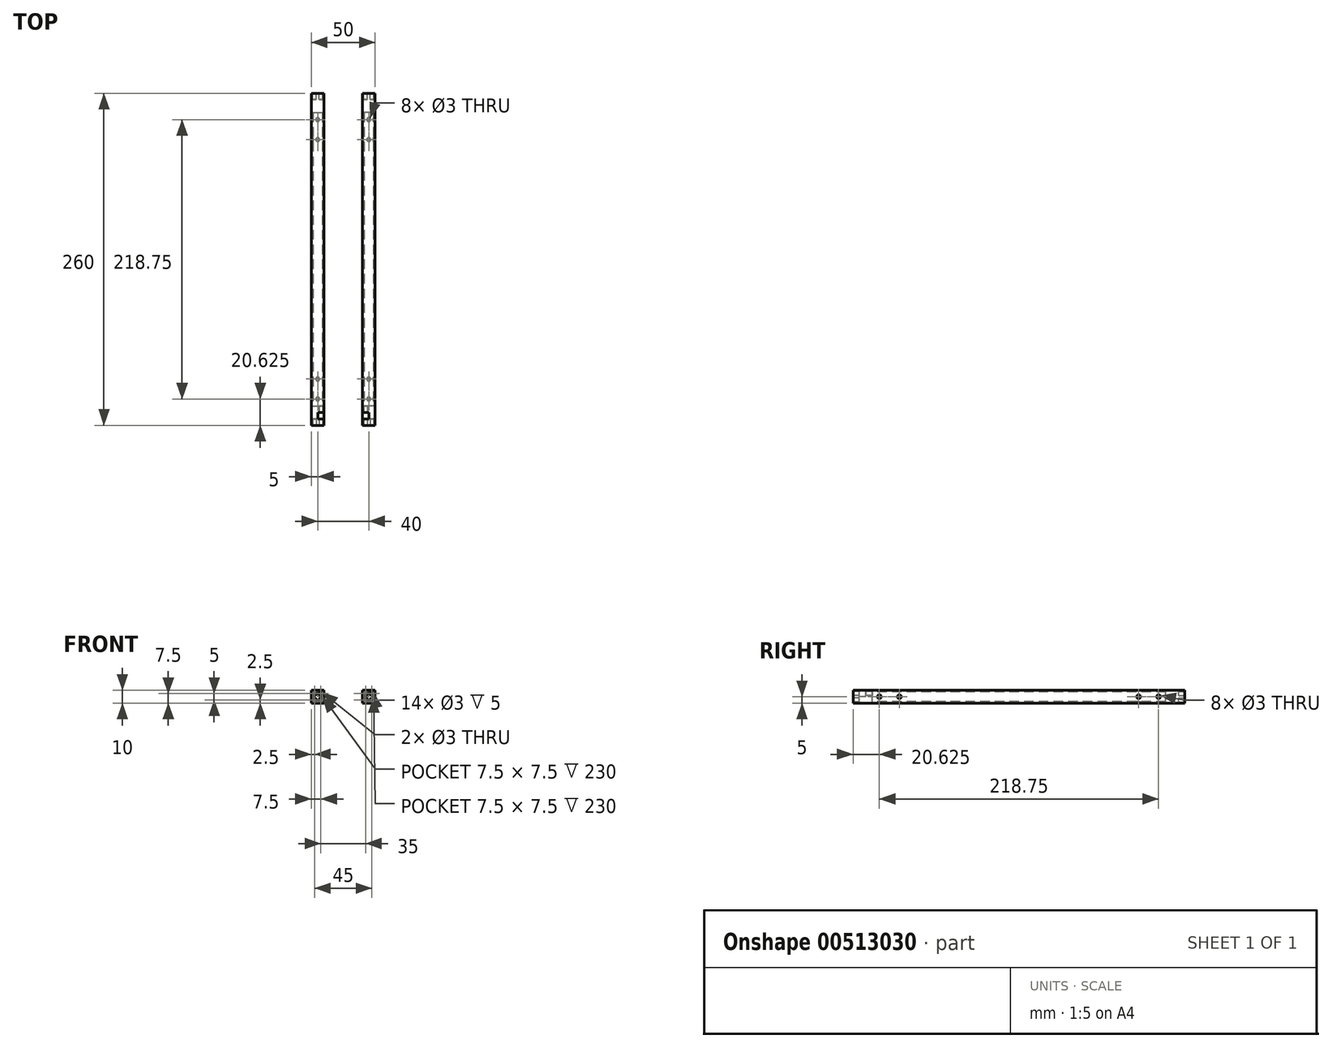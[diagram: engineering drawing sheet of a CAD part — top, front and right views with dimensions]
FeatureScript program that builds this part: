
annotation { "Feature Type Name" : "Feature", "Feature Type Description" : "" }
export const myFeature = defineFeature(function(context is Context, id is Id, definition is map)
    precondition{}
    {
        {
            var Q0;
            Q0=qCreatedBy(makeId("Front.planeOp"),FACE);
            var sketch = newSketch(context, id + "F0", { "sketchPlane" : qUnion([Q0])});
            skLineSegment(sketch, "E0.bottom", {"start": v(0, 0) * mm, "end": v(-10, 0) * mm});
            skLineSegment(sketch, "E0.top", {"start": v(0, 10) * mm, "end": v(-10, 10) * mm});
            skLineSegment(sketch, "E0.left", {"start": v(0, 0) * mm, "end": v(0, 10) * mm});
            skLineSegment(sketch, "E0.right", {"start": v(-10, 0) * mm, "end": v(-10, 10) * mm});
            skLineSegment(sketch, "E1.bottom", {"start": v(-1.25, 1.25) * mm, "end": v(-8.75, 1.25) * mm});
            skLineSegment(sketch, "E1.top", {"start": v(-1.25, 8.75) * mm, "end": v(-8.75, 8.75) * mm});
            skLineSegment(sketch, "E1.left", {"start": v(-1.25, 1.25) * mm, "end": v(-1.25, 8.75) * mm});
            skLineSegment(sketch, "E1.right", {"start": v(-8.75, 1.25) * mm, "end": v(-8.75, 8.75) * mm});
            skPoint(sketch, "E1.middle", {"position": v(-5, 5) * mm});
            skPoint(sketch, "E1.middle.positionSnap0", {"position": v(0, 5) * mm});
            skPoint(sketch, "E1.middle.positionSnap1", {"position": v(-5, 10) * mm});
            skPoint(sketch, "E1.centerSnap0", {"position": v(0, 5) * mm});
            skPoint(sketch, "E1.centerSnap1", {"position": v(-5, 10) * mm});
            skSolve(sketch);
        }
        {
            var Q0;
            Q0=makeQuery(id+"F0.imprint","IMPRINT",FACE,{"disambiguationData":[TD([[makeQuery(id+"F0.imprint","IMPRINT",EDGE,{"derivedFrom":sQuery(id+"F0.wireOp",EDGE,"E0.bottom")}),-1.0]])]});
            extrude(context, id + "F1", {"entities" : qUnion([Q0]), "oppositeDirection" : true, "depth" : 250 * mm});
        }
        {
            var Q0;
            Q0=makeQuery(id+"F0.imprint","IMPRINT",FACE,{"disambiguationData":[TD([[makeQuery(id+"F0.imprint","IMPRINT",EDGE,{"derivedFrom":sQuery(id+"F0.wireOp",EDGE,"E1.bottom")}),-1.0]])]});
            var Q1;
            Q1=makeQuery(id+"F0.imprint","IMPRINT",FACE,{"disambiguationData":[TD([[makeQuery(id+"F0.imprint","IMPRINT",EDGE,{"derivedFrom":sQuery(id+"F0.wireOp",EDGE,"E0.bottom")}),-1.0]])]});
            extrude(context, id + "F2", {"entities" : qUnion([Q0, Q1]), "operationType" : NewBodyOperationType.ADD, "depth" : 5 * mm});
        }
        {
            var Q0;
            Q0=makeQuery(id+"F2.opExtrude","CAP_FACE",FACE,{"disambiguationData":[OSD([sQuery(id+"F0.wireOp",EDGE,"E0.bottom"),sQuery(id+"F0.wireOp",EDGE,"E0.top"),sQuery(id+"F0.wireOp",EDGE,"E0.left"),sQuery(id+"F0.wireOp",EDGE,"E0.right")])],"isStart":false});
            var sketch = newSketch(context, id + "F3", { "sketchPlane" : qUnion([Q0])});
            skLineSegment(sketch, "E2", {"start": v(-5, 10) * mm, "end": v(-5, 5) * mm});
            skPoint(sketch, "E2.endSnap0", {"position": v(0, 5) * mm});
            skLineSegment(sketch, "E3", {"start": v(-5, 5) * mm, "end": v(0, 5) * mm});
            skLineSegment(sketch, "E4", {"start": v(-5, 5) * mm, "end": v(-5, 0) * mm});
            skLineSegment(sketch, "E5", {"start": v(-5, 5) * mm, "end": v(-10, 5) * mm});
            skCircle(sketch, "E6", {"center": v(-2.5, 7.5) * mm, "radius": 1.5 * mm});
            skPoint(sketch, "E6.centerSnap0", {"position": v(-2.5, 5) * mm});
            skPoint(sketch, "E6.centerSnap1", {"position": v(-5, 7.5) * mm});
            skCircle(sketch, "E7", {"center": v(-2.5, 2.5) * mm, "radius": 1.5 * mm});
            skPoint(sketch, "E7.centerSnap0", {"position": v(-5, 2.5) * mm});
            skCircle(sketch, "E8", {"center": v(-7.5, 2.5) * mm, "radius": 1.5 * mm});
            skPoint(sketch, "E8.centerSnap0", {"position": v(-7.5, 5) * mm});
            skCircle(sketch, "E9", {"center": v(-7.5, 7.5) * mm, "radius": 1.5 * mm});
            skSolve(sketch);
        }
        {
            var Q0;
            {var subQ0=sQuery(id+"F0.wireOp",EDGE,"E0.top");Q0=makeQuery(id+"F2.boolean.opBoolean","MERGE",FACE,{"derivedFrom":[makeQuery(id+"F1.opExtrude","SWEPT_FACE",FACE,{"disambiguationData":[OSD([subQ0])]}),makeQuery(id+"F2.opExtrude","SWEPT_FACE",FACE,{"disambiguationData":[OSD([subQ0])]})]});}
            var sketch = newSketch(context, id + "F4", { "sketchPlane" : qUnion([Q0])});
            skLineSegment(sketch, "E10.bottom", {"start": v(0, 0) * mm, "end": v(-10, 0) * mm});
            skLineSegment(sketch, "E10.top", {"start": v(0, 250) * mm, "end": v(-10, 250) * mm});
            skLineSegment(sketch, "E10.left", {"start": v(0, 0) * mm, "end": v(0, 250) * mm});
            skLineSegment(sketch, "E10.right", {"start": v(-10, 0) * mm, "end": v(-10, 250) * mm});
            skLineSegment(sketch, "E11", {"start": v(0, 125) * mm, "end": v(-10, 125) * mm});
            skSolve(sketch);
        }
        {
            var Q0;
            {var subQ0=sQuery(id+"F4.wireOp",EDGE,"E10.top");Q0=makeQuery(id+"F4.imprint","IMPRINT",FACE,{"disambiguationData":[TD([[makeQuery(id+"F4.imprint","IMPRINT",EDGE,{"derivedFrom":subQ0}),1.0]])]});}
            extrude(context, id + "F5", {"entities" : qUnion([Q0]), "operationType" : NewBodyOperationType.REMOVE, "oppositeDirection" : true, "depth" : 25 * mm});
        }
        {
            var Q0;
            Q0=makeQuery(id+"F3.imprint","IMPRINT",FACE,{"disambiguationData":[TD([[makeQuery(id+"F3.imprint","IMPRINT",EDGE,{"derivedFrom":sQuery(id+"F3.wireOp",EDGE,"E7")}),1.0]])]});
            var Q1;
            Q1=makeQuery(id+"F3.imprint","IMPRINT",FACE,{"disambiguationData":[TD([[makeQuery(id+"F3.imprint","IMPRINT",EDGE,{"derivedFrom":sQuery(id+"F3.wireOp",EDGE,"E6")}),1.0]])]});
            var Q2;
            Q2=makeQuery(id+"F3.imprint","IMPRINT",FACE,{"disambiguationData":[TD([[makeQuery(id+"F3.imprint","IMPRINT",EDGE,{"derivedFrom":sQuery(id+"F3.wireOp",EDGE,"E8")}),1.0]])]});
            extrude(context, id + "F6", {"entities" : qUnion([Q0, Q1, Q2]), "operationType" : NewBodyOperationType.REMOVE, "oppositeDirection" : true, "depth" : 5 * mm});
        }
        {
            var Q0;
            Q0=makeQuery(id+"F0.imprint","IMPRINT",FACE,{"disambiguationData":[TD([[makeQuery(id+"F0.imprint","IMPRINT",EDGE,{"derivedFrom":sQuery(id+"F0.wireOp",EDGE,"E1.bottom")}),-1.0]])]});
            extrude(context, id + "F7", {"entities" : qUnion([Q0]), "operationType" : NewBodyOperationType.ADD, "oppositeDirection" : true, "depth" : 10 * mm});
        }
        {
            var Q0;
            {var subQ0=sQuery(id+"F0.wireOp",EDGE,"E0.left");Q0=makeQuery(id+"F2.boolean.opBoolean","MERGE",FACE,{"derivedFrom":[makeQuery(id+"F1.opExtrude","SWEPT_FACE",FACE,{"disambiguationData":[OSD([subQ0])]}),makeQuery(id+"F2.opExtrude","SWEPT_FACE",FACE,{"disambiguationData":[OSD([subQ0])]})]});}
            var sketch = newSketch(context, id + "F8", { "sketchPlane" : qUnion([Q0])});
            skLineSegment(sketch, "E12.bottom", {"start": v(0, 0) * mm, "end": v(125, 0) * mm});
            skLineSegment(sketch, "E12.top", {"start": v(62.5, 10) * mm, "end": v(125, 10) * mm});
            skLineSegment(sketch, "E12.left", {"start": v(0, 0) * mm, "end": v(0, 10) * mm});
            skLineSegment(sketch, "E12.right", {"start": v(125, 0) * mm, "end": v(125, 10) * mm});
            skLineSegment(sketch, "E13", {"start": v(62.5, 10) * mm, "end": v(62.5, 0) * mm});
            skLineSegment(sketch, "E14", {"start": v(62.5, 10) * mm, "end": v(0, 10) * mm});
            skCircle(sketch, "E15", {"center": v(31.25, 5) * mm, "radius": 1.5 * mm});
            skPoint(sketch, "E15.centerSnap0", {"position": v(0, 5) * mm});
            skPoint(sketch, "E15.centerSnap1", {"position": v(31.25, 10) * mm});
            skLineSegment(sketch, "E16", {"start": v(31.25, 10) * mm, "end": v(0, 10) * mm});
            skCircle(sketch, "E17", {"center": v(15.62, 5) * mm, "radius": 1.5 * mm});
            skPoint(sketch, "E17.centerSnap0", {"position": v(15.62, 10) * mm});
            skSolve(sketch);
        }
        {
            var Q0;
            Q0=makeQuery(id+"F8.imprint","IMPRINT",FACE,{"disambiguationData":[TD([[makeQuery(id+"F8.imprint","IMPRINT",EDGE,{"derivedFrom":sQuery(id+"F8.wireOp",EDGE,"E17")}),1.0]])]});
            var Q1;
            Q1=makeQuery(id+"F8.imprint","IMPRINT",FACE,{"disambiguationData":[TD([[makeQuery(id+"F8.imprint","IMPRINT",EDGE,{"derivedFrom":sQuery(id+"F8.wireOp",EDGE,"E15")}),1.0]])]});
            extrude(context, id + "F9", {"entities" : qUnion([Q0, Q1]), "operationType" : NewBodyOperationType.REMOVE, "oppositeDirection" : true, "depth" : 5 * mm});
        }
        {
            var Q0;
            {var subQ0=sQuery(id+"F0.wireOp",EDGE,"E0.bottom");Q0=makeQuery(id+"F2.boolean.opBoolean","MERGE",FACE,{"derivedFrom":[makeQuery(id+"F1.opExtrude","SWEPT_FACE",FACE,{"disambiguationData":[OSD([subQ0])]}),makeQuery(id+"F2.opExtrude","SWEPT_FACE",FACE,{"disambiguationData":[OSD([subQ0])]})]});}
            var sketch = newSketch(context, id + "F10", { "sketchPlane" : qUnion([Q0])});
            skLineSegment(sketch, "E18.bottom", {"start": v(-10, 0) * mm, "end": v(-10, -125) * mm});
            skLineSegment(sketch, "E18.top", {"start": v(0, -62.5) * mm, "end": v(0, -125) * mm});
            skLineSegment(sketch, "E18.left", {"start": v(-10, 0) * mm, "end": v(0, 0) * mm});
            skLineSegment(sketch, "E18.right", {"start": v(-10, -125) * mm, "end": v(0, -125) * mm});
            skLineSegment(sketch, "E19", {"start": v(0, -62.5) * mm, "end": v(-10, -62.5) * mm});
            skLineSegment(sketch, "E20", {"start": v(0, -62.5) * mm, "end": v(0, 0) * mm});
            skCircle(sketch, "E21", {"center": v(-5, -31.25) * mm, "radius": 1.5 * mm});
            skPoint(sketch, "E21.centerSnap0", {"position": v(-5, 0) * mm});
            skPoint(sketch, "E21.centerSnap1", {"position": v(0, -31.25) * mm});
            skLineSegment(sketch, "E22", {"start": v(0, -31.25) * mm, "end": v(0, 0) * mm});
            skCircle(sketch, "E23", {"center": v(-5, -15.62) * mm, "radius": 1.5 * mm});
            skPoint(sketch, "E23.centerSnap0", {"position": v(0, -15.62) * mm});
            skSolve(sketch);
        }
        {
            var Q0;
            Q0=makeQuery(id+"F10.imprint","IMPRINT",FACE,{"disambiguationData":[TD([[makeQuery(id+"F10.imprint","IMPRINT",EDGE,{"derivedFrom":sQuery(id+"F10.wireOp",EDGE,"E21")}),1.0]])]});
            var Q1;
            Q1=makeQuery(id+"F10.imprint","IMPRINT",FACE,{"disambiguationData":[TD([[makeQuery(id+"F10.imprint","IMPRINT",EDGE,{"derivedFrom":sQuery(id+"F10.wireOp",EDGE,"E23")}),1.0]])]});
            extrude(context, id + "F11", {"entities" : qUnion([Q0, Q1]), "operationType" : NewBodyOperationType.REMOVE, "oppositeDirection" : true, "depth" : 5 * mm});
        }
        {
            var Q0;
            Q0=makeQuery(id+"F1.opExtrude","SWEPT_BODY",BODY,{"disambiguationData":[OSD([sQuery(id+"F0.wireOp",EDGE,"E0.bottom"),sQuery(id+"F0.wireOp",EDGE,"E0.top"),sQuery(id+"F0.wireOp",EDGE,"E0.left"),sQuery(id+"F0.wireOp",EDGE,"E0.right"),sQuery(id+"F0.wireOp",EDGE,"E1.bottom"),sQuery(id+"F0.wireOp",EDGE,"E1.top"),sQuery(id+"F0.wireOp",EDGE,"E1.left"),sQuery(id+"F0.wireOp",EDGE,"E1.right")])]});
            var Q1;
            Q1=makeQuery(id+"F5.boolean.opBoolean","COPY",FACE,{"derivedFrom":makeQuery(id+"F5.opExtrude","SWEPT_FACE",FACE,{"disambiguationData":[OSD([sQuery(id+"F4.wireOp",EDGE,"E11")])]})});
            mirror(context, id + "F12", {"operationType" : NewBodyOperationType.ADD, "entities" : qUnion([Q0]), "mirrorPlane" : qUnion([Q1])});
        }
        {
            var Q0;
            {var subQ0=sQuery(id+"F0.wireOp",EDGE,"E0.top");var subQ1=makeQuery(id+"F2.boolean.opBoolean","MERGE",FACE,{"derivedFrom":[makeQuery(id+"F1.opExtrude","SWEPT_FACE",FACE,{"disambiguationData":[OSD([subQ0])]}),makeQuery(id+"F2.opExtrude","SWEPT_FACE",FACE,{"disambiguationData":[OSD([subQ0])]})]});Q0=makeQuery(id+"F12.boolean.opBoolean","MERGE",FACE,{"derivedFrom":[subQ1,makeQuery(id+"F12.opPattern","COPY",FACE,{"derivedFrom":subQ1,"instanceName":"1"})]});}
            var sketch = newSketch(context, id + "F13", { "sketchPlane" : qUnion([Q0])});
            skLineSegment(sketch, "E24", {"start": v(-10, -5) * mm, "end": v(-10, 0) * mm});
            skLineSegment(sketch, "E25", {"start": v(-10, 0) * mm, "end": v(-5, 0) * mm});
            skLineSegment(sketch, "E26", {"start": v(-5, 0) * mm, "end": v(-5, 5) * mm});
            skLineSegment(sketch, "E27", {"start": v(-5, 5) * mm, "end": v(-10, 5) * mm});
            skSolve(sketch);
        }
        {
            var Q0;
            {var subQ0=sQuery(id+"F13.wireOp",EDGE,"E25");Q0=makeQuery(id+"F13.imprint","IMPRINT",FACE,{"disambiguationData":[TD([[makeQuery(id+"F13.imprint","IMPRINT",EDGE,{"derivedFrom":subQ0}),1.0]])]});}
            extrude(context, id + "F14", {"entities" : qUnion([Q0]), "operationType" : NewBodyOperationType.REMOVE, "oppositeDirection" : true, "depth" : 5 * mm});
        }
        {
            var Q0;
            Q0=makeQuery(id+"F3.imprint","IMPRINT",FACE,{"disambiguationData":[TD([[makeQuery(id+"F3.imprint","IMPRINT",EDGE,{"derivedFrom":sQuery(id+"F3.wireOp",EDGE,"E9")}),1.0]])]});
            extrude(context, id + "F15", {"entities" : qUnion([Q0]), "operationType" : NewBodyOperationType.REMOVE, "oppositeDirection" : true, "depth" : 15 * mm});
        }
        {
            var Q0;
            Q0=makeQuery(id+"F1.opExtrude","SWEPT_BODY",BODY,{"disambiguationData":[OSD([sQuery(id+"F0.wireOp",EDGE,"E0.bottom"),sQuery(id+"F0.wireOp",EDGE,"E0.top"),sQuery(id+"F0.wireOp",EDGE,"E0.left"),sQuery(id+"F0.wireOp",EDGE,"E0.right"),sQuery(id+"F0.wireOp",EDGE,"E1.bottom"),sQuery(id+"F0.wireOp",EDGE,"E1.top"),sQuery(id+"F0.wireOp",EDGE,"E1.left"),sQuery(id+"F0.wireOp",EDGE,"E1.right")])]});
            var Q1;
            {var subQ0=sQuery(id+"F0.wireOp",EDGE,"E0.right");var subQ1=makeQuery(id+"F2.boolean.opBoolean","MERGE",FACE,{"derivedFrom":[makeQuery(id+"F1.opExtrude","SWEPT_FACE",FACE,{"disambiguationData":[OSD([subQ0])]}),makeQuery(id+"F2.opExtrude","SWEPT_FACE",FACE,{"disambiguationData":[OSD([subQ0])]})]});Q1=makeQuery(id+"F12.boolean.opBoolean","MERGE",FACE,{"derivedFrom":[subQ1,makeQuery(id+"F12.opPattern","COPY",FACE,{"derivedFrom":subQ1,"instanceName":"1"})]});}
            mirror(context, id + "F16", {"entities" : qUnion([Q0]), "mirrorPlane" : qUnion([Q1])});
        }
        {
            var Q0;
            Q0=makeQuery(id+"F16.opPattern","COPY",BODY,{"derivedFrom":makeQuery(id+"F1.opExtrude","SWEPT_BODY",BODY,{"disambiguationData":[OSD([sQuery(id+"F0.wireOp",EDGE,"E0.bottom"),sQuery(id+"F0.wireOp",EDGE,"E0.top"),sQuery(id+"F0.wireOp",EDGE,"E0.left"),sQuery(id+"F0.wireOp",EDGE,"E0.right"),sQuery(id+"F0.wireOp",EDGE,"E1.bottom"),sQuery(id+"F0.wireOp",EDGE,"E1.top"),sQuery(id+"F0.wireOp",EDGE,"E1.left"),sQuery(id+"F0.wireOp",EDGE,"E1.right")])]}),"instanceName":"1"});
            transform(context, id + "F17", {"entities" : qUnion([Q0]), "transformType" : TransformType.TRANSLATION_3D, "dx" : -30 * mm, "dy" : 0 * mm, "dz" : 0 * mm, "makeCopy" : false});
        }
    });
